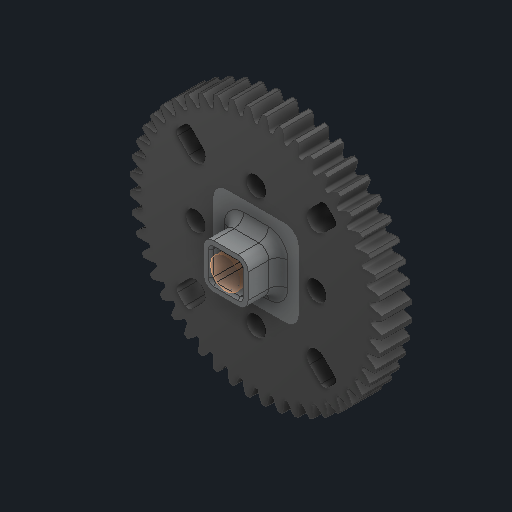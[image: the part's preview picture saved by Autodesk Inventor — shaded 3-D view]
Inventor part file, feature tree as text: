
AUTODESK INVENTOR PART (.ipt)
format: ipt  version: 2025 (Build 290162000, 162)  size: 2,524,672 bytes
history: native  units: in
note: dims shown in document units (in); Inventor stores cm internally (conversion verified against a paired STEP export)
features: other x6, sketch x2
ambient origin geometry x8: Origin, YZ Plane, XZ Plane, XY Plane, X Axis, Y Axis, Z Axis, Center Point
bodies: Solid1 (feature_tree), Solid2 (feature_tree)
feature tree (8):
  other  "Half Cut HS 48T Gear, No Insert.ipt"
  other  "Solid1::Half Cut HS 48T Gear, No Insert.ipt"
  other  "Solid2::Half Cut HS 48T Gear, No Insert.ipt"
  other  "TaggingFeature1"
  sketch  "Sketch1"  dims[d0=0.3937in]
  sketch  "Sketch2"
  other  "Srf1"
  other  "Srf1::Derived"
